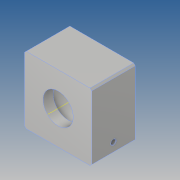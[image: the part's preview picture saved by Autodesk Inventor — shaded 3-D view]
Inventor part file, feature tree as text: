
AUTODESK INVENTOR PART (.ipt)
format: ipt  version: 2018.2 (Build 222227000, 227)  size: 237,056 bytes
history: native  units: mm
features: sketch x7, hole x3, chamfer x3, other x2, projected_geometry x2, extrude x1, mirror x1
ambient origin geometry x8: Origin, YZ Plane, XZ Plane, XY Plane, X Axis, Y Axis, Z Axis, Center Point
bodies: Volumenkörper1 (feature_tree)
feature tree (19):
  extrude  "Grundkoerper"  Depth=100.0mm
  sketch  "Skizze2"  dims[d5=65.0mm d6=0.0mm d8=0.0mm]
  other  "Arbeitsachse1"
  other  "Lagersitz"
  sketch  "Skizze_Lagersitz"  dims[d94=50.0mm d95=15.0mm d96=6.647mm d97=16.0mm d98=8.0mm d99=2.0mm d100=90.0deg d101=22.2mm d102=20.594885mm d160=75.0mm d161=30.0mm d167=85.0mm d168=60.0mm d170=360.0deg d172=4.134mm d173=10.0mm d174=5.0mm d175=2.0mm d176=90.0deg d177=14.2mm d178=20.594885mm d181=76.0mm d182=15.0mm d183=12.0mm d184=6.647mm d185=16.0mm d186=4.0mm d187=2.0mm d188=90.0deg d189=22.2mm d190=20.594885mm]
  hole  "M5x10_Deckel"  [1 undecoded]
  hole  "M8x16_Seite"  [1 undecoded]
  mirror  "M8x16_Seite_Spiegel"
  hole  "M8x16_Boden"  [1 undecoded]
  chamfer  "Fase_Lagersitz"  Distance=0.25mm Angle=45.0deg
  chamfer  "Fase_Deckel"  Distance=1.0mm Angle=45.0deg
  chamfer  "Fase_Allgemein"  Distance=2.5mm Angle=45.0deg
  sketch  "Skizze1"  dims[d1=100.0mm d3=100.0mm]
  sketch  "Skizze3"  dims[d9=45.0mm d10=72.0mm]
  projected_geometry  "Projizierte Kontur2"
  sketch  "Skizze9"  dims[d33=5.0mm]
  projected_geometry  "Projizierte Kontur3"
  sketch  "Skizze5"  dims[d11=45.0mm d12=90.0deg]
  sketch  "Skizze16"  dims[d34=62.0mm d52=0.25mm d53=2.0mm d54=45.0deg d58=1.0mm d59=2.0mm d60=45.0deg d78=2.5mm d79=2.0mm d80=45.0deg]
note: 3 required parameter values undecoded (feature->parameter linkage not recoverable at this tier; creation-order binding heuristic only, values carry confidence <= 0.55)
